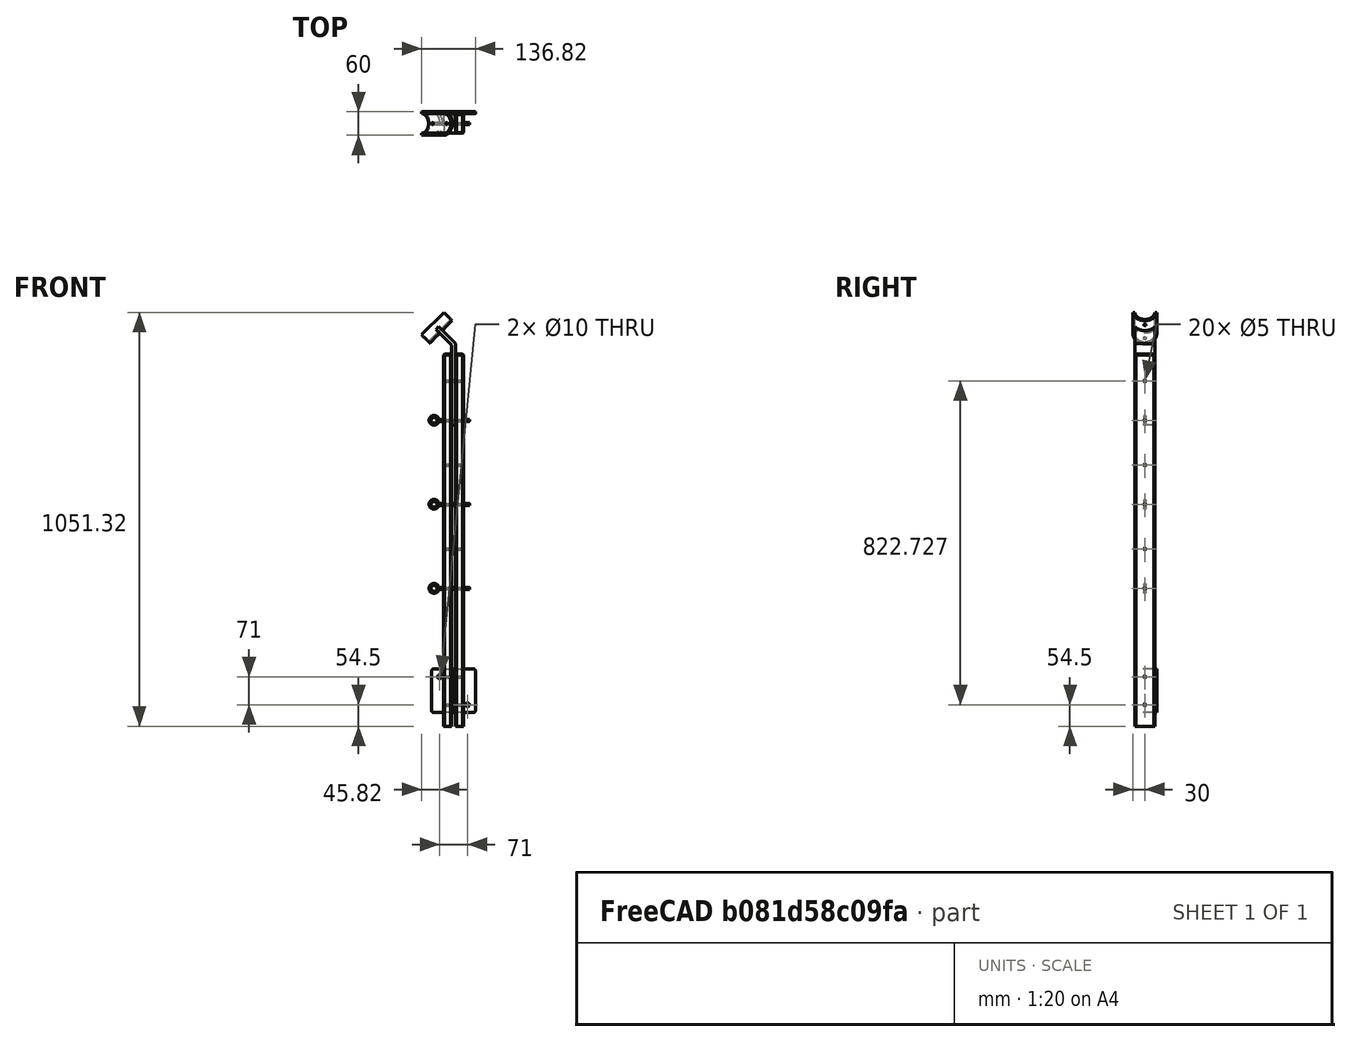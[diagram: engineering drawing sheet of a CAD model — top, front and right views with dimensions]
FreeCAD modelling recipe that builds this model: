
FCSTD DOCUMENT  (FreeCAD 0.17R10885 (Git))
Label: railing_last_element
License: All rights reserved
LicenseURL: http://en.wikipedia.org/wiki/All_rights_reserved
objects: Part::FeaturePython×7, Part::Part2DObjectPython×4, Part::Compound×4, Part::Cylinder×2, Part::Feature×1, App::Part×1, Part::Box×1, Part::Cut×1
note: 20 computed .brp shape members not serialized (recipe doc carries the construction recipe); baked Part::Feature solids carry a one-line shape summary decoded from their .brp

FEATURE [Part::Feature] Compound001_cs
  Placement = pos=(-77.8923,0,-170) rot=(0,0,1;0rad)
  shape: bbox 1490 x 3e-07 x 1728 mm, 0 faces, 0 solids (baked)
FEATURE [Part::Part2DObjectPython] Line  # Draft 2D object (typed FeaturePython)
  ChamferSize = 0
  Closed = false
  End = (-35.6937,-365,-86.0859)
  FilletRadius = 0
  Length = 220.312
  MakeFace = true
  Points = (2) [(-191.478,-365,69.6984),(-35.6937,-365,-86.0859)]
  Start = (-191.478,-365,69.6984)
  Subdivisions = 0
FEATURE [Part::Part2DObjectPython] Line001  # Draft 2D object (typed FeaturePython)
  ChamferSize = 0
  Closed = false
  End = (708.599,-365,658.207)
  FilletRadius = 0
  Length = 220.312
  MakeFace = true
  Points = (2) [(552.815,-365,813.991),(708.599,-365,658.207)]
  Start = (552.815,-365,813.991)
  Subdivisions = 0
FEATURE [Part::Part2DObjectPython] Line002  # Draft 2D object (typed FeaturePython)
  ChamferSize = 0
  Closed = false
  End = (630.707,-30,736.099)
  FilletRadius = 0
  Length = 1052.59
  MakeFace = true
  Points = (2) [(-113.586,-30,-8.19375),(630.707,-30,736.099)]
  Start = (-113.586,-30,-8.19375)
  Subdivisions = 0
FEATURE [Part::FeaturePython] railing_wood_002  # a2plus imported part (geometry in sourceFile) (typed FeaturePython)
  fixedPosition = true
  sourceFile = railing_wood.fcstd
  timeLastImport = 1.49253e+09
  updateColors = true
FEATURE [Part::FeaturePython] test_002  label="handrail_holder001"  # a2plus imported part (geometry in sourceFile) (typed FeaturePython)
  Placement = pos=(0,-3.2e-11,1000) rot=(0,0,1;0rad)
  fixedPosition = false
  sourceFile = handrail_holder.fcstd
  timeLastImport = 1.49254e+09
  updateColors = true
FEATURE [Part::FeaturePython] railing_plate_003  # a2plus imported part (geometry in sourceFile) (typed FeaturePython)
  Placement = pos=(4e-11,30,145) rot=(0,0,1;0rad)
  fixedPosition = false
  sourceFile = railing_plate.fcstd
  timeLastImport = 1.49258e+09
  updateColors = true
FEATURE [Part::Cylinder] Cylinder005  label="Cylinder008"
  Angle = 360
  AttacherType = Attacher::AttachEngine3D
  Height = 100
  Placement = pos=(-50,0,-35.5) rot=(0,1,0;1.5708rad)
  Radius = 2.5
FEATURE [Part::FeaturePython] eyelet_01  # a2plus imported part (geometry in sourceFile) (typed FeaturePython)
  Placement = pos=(-49.689,0,0) rot=(0,0,1;0rad)
  fixedPosition = false
  sourceFile = eyelet.fcstd
  timeLastImport = 1.49253e+09
  updateColors = true
FEATURE [Part::Compound] Compound005
  Links = -> [eyelet_01]
  Placement = pos=(0,0,405.269) rot=(0,0,1;0rad)
FEATURE [Part::FeaturePython] Array  # Draft array (typed FeaturePython)
  Angle = 360
  ArrayType = 0
  Axis = (0,0,1)
  Base = -> Compound005
  Center = (0,0,0)
  Fuse = false
  IntervalAxis = (0,0,0)
  IntervalX = (0,0,213.479)
  IntervalY = (0,0,0)
  IntervalZ = (0,0,0)
  NumberPolar = 1
  NumberX = 3
  NumberY = 1
  NumberZ = 1
  expr: IntervalX.z = rope_vertical_offset.Length
FEATURE [Part::Part2DObjectPython] Line011  label="rope_vertical_offset"  # Draft 2D object (typed FeaturePython)
  ChamferSize = 0
  Closed = false
  End = (-50,0,191.79)
  FilletRadius = 0
  Length = 213.479
  MakeFace = true
  Points = (2) [(-50,-6.82854e-15,405.269),(-50,-6.82854e-15,191.79)]
  Start = (-50,0,405.269)
  Subdivisions = 0
FEATURE [App::Part] Part  label="drawing"
  Group = -> [Line,Line001,Line002,Compound001_cs,Line011]
  License = CC BY 3.0
  LicenseURL = http://creativecommons.org/licenses/by/3.0/
  Origin = -> PartOrigin
FEATURE [Part::Cylinder] Cylinder006  label="Cylinder"
  Angle = 360
  AttacherType = Attacher::AttachEngine3D
  Height = 100
  Placement = pos=(-50,0,405.269) rot=(0,1,0;1.5708rad)
  Radius = 2.5
FEATURE [Part::FeaturePython] Array001  # Draft array (typed FeaturePython)
  Angle = 360
  ArrayType = 0
  Axis = (0,0,1)
  Base = -> Cylinder006
  Center = (0,0,0)
  Fuse = false
  IntervalAxis = (0,0,0)
  IntervalX = (0,0,100)
  IntervalY = (0,0,0)
  IntervalZ = (0,0,213.479)
  NumberPolar = 1
  NumberX = 2
  NumberY = 1
  NumberZ = 3
FEATURE [Part::FeaturePython] Component  label="Cylinder006"  # WARN: FeaturePython — macro-defined, semantics opaque (R4)
  CloneOf = -> Cylinder005
  HorizontalArea = 0
  MoveWithHost = false
  PerimeterLength = 0
  Placement = pos=(-50,0,35.5) rot=(0,1,0;1.5708rad)
  Role = 0
  VerticalArea = 0
FEATURE [Part::Compound] Compound006
  Links = -> [Cylinder005,Component]
  Placement = pos=(0,0,145) rot=(0,0,1;0rad)
  expr: Placement.Base.z = railing_plate_003.Placement.Base.z
FEATURE [Part::Box] Box001  label="Cube001"
  AttacherType = Attacher::AttachEngine3D
  Height = 100
  Length = 200
  Placement = pos=(-75,-125,-45) rot=(0,0,1;0rad)
  Width = 200
FEATURE [Part::Compound] Compound004
  Links = -> [Array001,Compound006,Box001]
FEATURE [Part::Cut] Cut001
  Base = -> railing_wood_002
  Tool = -> Compound004
FEATURE [Part::Compound] Compound003  label="Railing_element001"
  Links = -> [Cut001,test_002,railing_plate_003,Array]
  Placement = pos=(0,0,4.71e-10) rot=(0,0,1;0rad)
